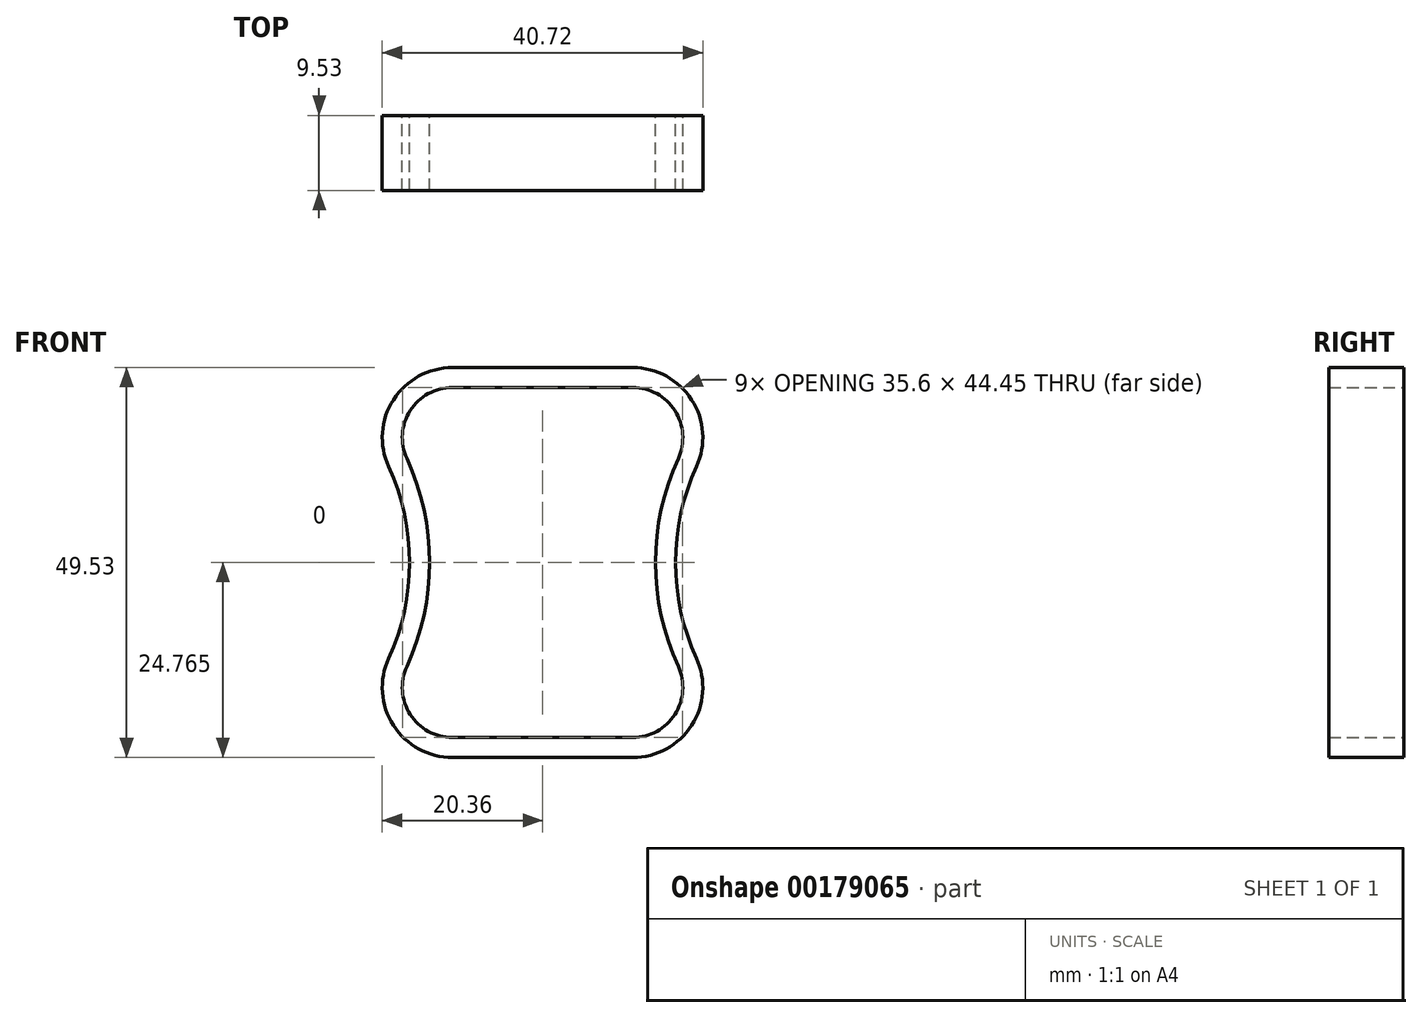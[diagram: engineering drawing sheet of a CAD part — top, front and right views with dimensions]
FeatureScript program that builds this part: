
annotation { "Feature Type Name" : "Feature", "Feature Type Description" : "" }
export const myFeature = defineFeature(function(context is Context, id is Id, definition is map)
    precondition{}
    {
        {
            var Q0;
            Q0=qCreatedBy(makeId("Front.planeOp"),FACE);
            var sketch = newSketch(context, id + "F0", { "sketchPlane" : qUnion([Q0])});
            skLineSegment(sketch, "E0", {"start": v(0, 0) * mm, "end": v(0, 62.24) * mm, "construction": true});
            skLineSegment(sketch, "E1", {"start": v(0, 0) * mm, "end": v(-11.47, 0) * mm});
            skLineSegment(sketch, "E2", {"start": v(-11.47, 44.45) * mm, "end": v(0, 44.45) * mm});
            skArc(sketch, "E3", {"start": v(-17.24, 9) * mm, "mid": v(-14.35, 22.23) * mm, "end": v(-17.24, 35.45) * mm});
            skLineSegment(sketch, "E4", {"start": v(-46.1, 22.23) * mm, "end": v(0, 22.23) * mm, "construction": true});
            skCircle(sketch, "E5", {"center": v(0, 22.23) * mm, "radius": 14.35 * mm, "construction": true});
            skPoint(sketch, "E6.visualSharp", {"position": v(-23.43, 44.45) * mm});
            skArc(sketch, "E6.filletArc", {"start": v(-11.47, 44.45) * mm, "mid": v(-16.81, 41.53) * mm, "end": v(-17.24, 35.45) * mm});
            skPoint(sketch, "E7.visualSharp", {"position": v(-23.43, 0) * mm});
            skArc(sketch, "E7.filletArc", {"start": v(-17.24, 9) * mm, "mid": v(-16.81, 2.92) * mm, "end": v(-11.47, 0) * mm});
            skLineSegment(sketch, "E8.MirrorCS", {"start": v(0, 0) * mm, "end": v(11.47, 0) * mm});
            skLineSegment(sketch, "E9.MirrorCS", {"start": v(11.47, 44.45) * mm, "end": v(0, 44.45) * mm});
            skArc(sketch, "E10.MirrorCS", {"start": v(17.24, 9) * mm, "mid": v(14.35, 22.23) * mm, "end": v(17.24, 35.45) * mm});
            skArc(sketch, "E11.MirrorCS", {"start": v(17.24, 9) * mm, "mid": v(16.81, 2.92) * mm, "end": v(11.47, 0) * mm});
            skArc(sketch, "E12.MirrorCS", {"start": v(11.47, 44.45) * mm, "mid": v(16.81, 41.53) * mm, "end": v(17.24, 35.45) * mm});
            skPoint(sketch, "E13.MirrorP", {"position": v(23.43, 0) * mm});
            skPoint(sketch, "E14.MirrorP", {"position": v(23.43, 44.45) * mm});
            skArc(sketch, "E15.0", {"start": v(-19.55, 10.05) * mm, "mid": v(-18.95, 1.55) * mm, "end": v(-11.47, -2.54) * mm});
            skArc(sketch, "E15.1", {"start": v(-19.55, 10.05) * mm, "mid": v(-16.9, 22.23) * mm, "end": v(-19.55, 34.4) * mm});
            skArc(sketch, "E15.2", {"start": v(-11.47, 47) * mm, "mid": v(-18.95, 42.9) * mm, "end": v(-19.55, 34.4) * mm});
            skLineSegment(sketch, "E16.0", {"start": v(0, -2.54) * mm, "end": v(-11.47, -2.54) * mm});
            skLineSegment(sketch, "E16.1", {"start": v(0, -2.54) * mm, "end": v(11.47, -2.54) * mm});
            skArc(sketch, "E16.2", {"start": v(19.55, 10.05) * mm, "mid": v(18.95, 1.55) * mm, "end": v(11.47, -2.54) * mm});
            skLineSegment(sketch, "E16.3", {"start": v(-11.47, 47) * mm, "end": v(0, 47) * mm});
            skLineSegment(sketch, "E16.4", {"start": v(11.47, 47) * mm, "end": v(0, 47) * mm});
            skArc(sketch, "E16.5", {"start": v(11.47, 47) * mm, "mid": v(18.95, 42.9) * mm, "end": v(19.55, 34.4) * mm});
            skArc(sketch, "E16.6", {"start": v(19.55, 10.05) * mm, "mid": v(16.9, 22.23) * mm, "end": v(19.55, 34.4) * mm});
            skSolve(sketch);
        }
        {
            var Q0;
            Q0 = qSketchRegion(id + "F0", true);
            extrude(context, id + "F1", {"entities" : qUnion([Q0]), "depth" : 9.52 * mm});
        }
    });
